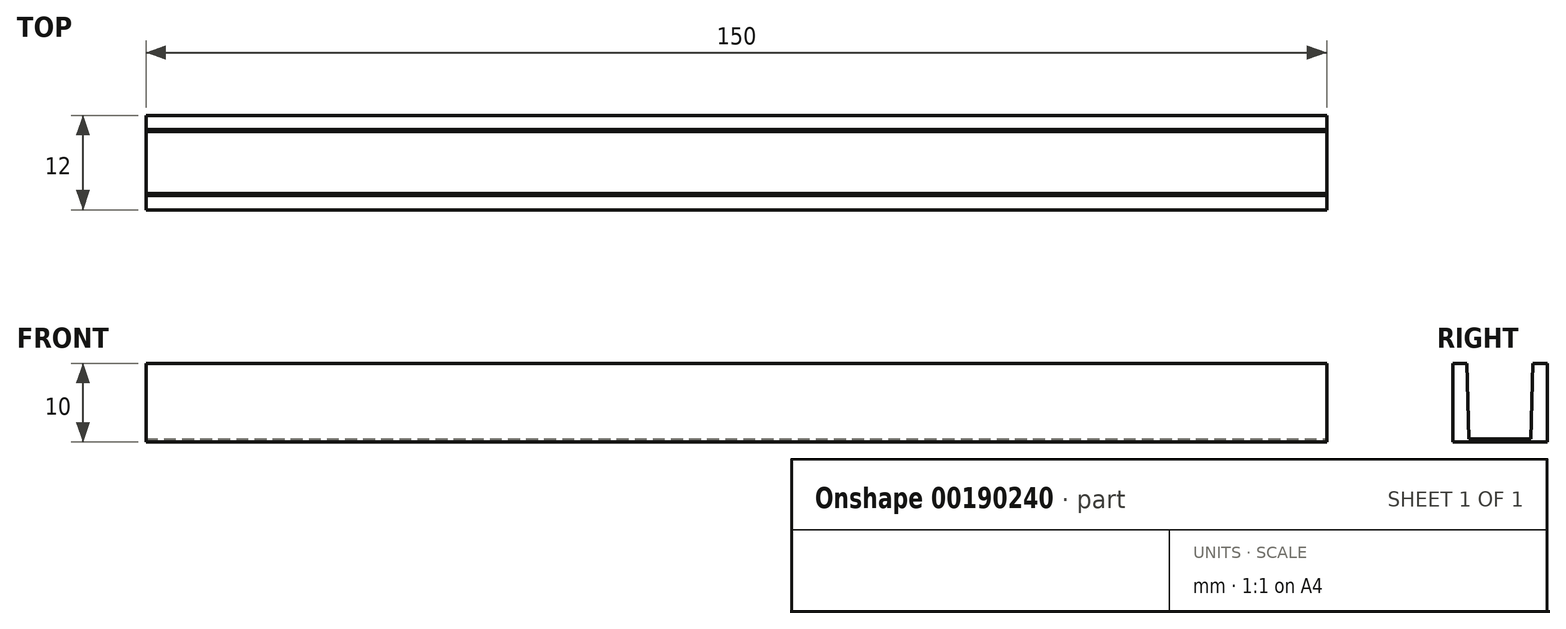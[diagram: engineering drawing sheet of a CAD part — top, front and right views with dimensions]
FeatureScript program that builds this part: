
annotation { "Feature Type Name" : "Feature", "Feature Type Description" : "" }
export const myFeature = defineFeature(function(context is Context, id is Id, definition is map)
    precondition{}
    {
        {
            var Q0;
            Q0=qCreatedBy(makeId("Top.planeOp"),FACE);
            var sketch = newSketch(context, id + "F0", { "sketchPlane" : qUnion([Q0])});
            skLineSegment(sketch, "E0", {"start": v(-75, 0) * mm, "end": v(75, 0) * mm});
            skSolve(sketch);
        }
        {
            var Q0;
            Q0=qCreatedBy(makeId("Right.planeOp"),FACE);
            var sketch = newSketch(context, id + "F1", { "sketchPlane" : qUnion([Q0])});
            skLineSegment(sketch, "E1", {"start": v(-6, 0) * mm, "end": v(6, 0) * mm});
            skLineSegment(sketch, "E2", {"start": v(6, 0) * mm, "end": v(6, 10) * mm});
            skLineSegment(sketch, "E3", {"start": v(6, 10) * mm, "end": v(4.2, 10) * mm});
            skLineSegment(sketch, "E4", {"start": v(4.2, 10) * mm, "end": v(3.95, 0.4) * mm});
            skLineSegment(sketch, "E5", {"start": v(3.95, 0.4) * mm, "end": v(-3.95, 0.4) * mm});
            skLineSegment(sketch, "E6", {"start": v(-3.95, 0.4) * mm, "end": v(-4.2, 10) * mm});
            skLineSegment(sketch, "E7", {"start": v(-4.2, 10) * mm, "end": v(-6, 10) * mm});
            skLineSegment(sketch, "E8", {"start": v(-6, 10) * mm, "end": v(-6, 0) * mm});
            skPoint(sketch, "E9", {"position": v(0, 0.4) * mm});
            skSolve(sketch);
        }
        {
            var Q0;
            Q0=makeQuery(id+"F1.imprint","IMPRINT",FACE,{"disambiguationData":[TD([[makeQuery(id+"F1.imprint","IMPRINT",EDGE,{"derivedFrom":sQuery(id+"F1.wireOp",EDGE,"E1")}),1.0]])]});
            var Q1;
            Q1=sQuery(id+"F0.wireOp",EDGE,"E0");
            sweep(context, id + "F2", {"profiles" : qUnion([Q0]), "path" : qUnion([Q1])});
        }
    });
